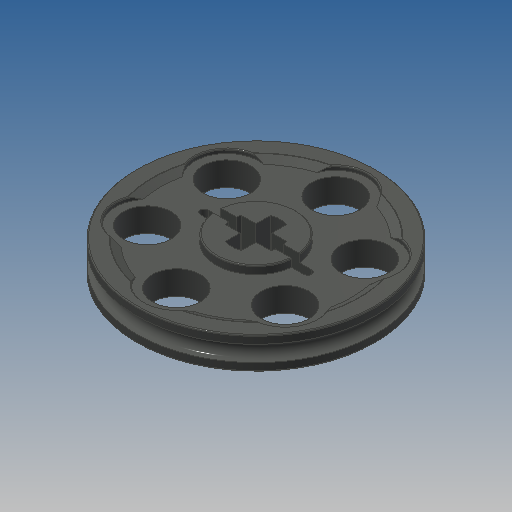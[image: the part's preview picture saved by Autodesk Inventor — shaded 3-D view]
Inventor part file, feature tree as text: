
AUTODESK INVENTOR PART (.ipt)
format: ipt  version: 2022.2 (Build 262287000, 287)  size: 430,080 bytes
history: native  units: in
note: dims shown in document units (in); Inventor stores cm internally (conversion verified against a paired STEP export)
features: extrude x3, sketch x2, revolve x1, mirror x1, pattern_circular x1, fillet x1
ambient origin geometry x8: Origin, YZ Plane, XZ Plane, XY Plane, X Axis, Y Axis, Z Axis, Center Point
bodies: Solid1 (feature_tree)
feature tree (9):
  revolve  "Revolution1"  [1 undecoded]
  sketch  "Sketch3"  dims[d2=0.315in d3=0.0945in d4=0.7559in d5=0.8189in d6=0.063in d7=0.126in d8=90.0deg d9=0.189in d10=0.252in d11=0.315in d12=0.189in d13=0.063in d14=0.4409in d15=0.0315in d16=0.3937in d17=0.0in d18=0.3937in d19=0.0in d20=0.3937in d21=0.0in d22=2.3622in d23=360.0deg d25=0.0039in]
  extrude  "Extrusion1"  Depth=0.0039in
  extrude  "Extrusion2"  Depth=0.0039in
  extrude  "Extrusion3"  Depth=0.0039in
  mirror  "Mirror1"
  pattern_circular  "Circular Pattern1"  [2 undecoded]
  fillet  "Fillet1"  Radius=0.126in
  sketch  "Sketch2"  dims[d0=0.1575in d1=0.9449in]
note: 3 required parameter values undecoded (feature->parameter linkage not recoverable at this tier; creation-order binding heuristic only, values carry confidence <= 0.55)